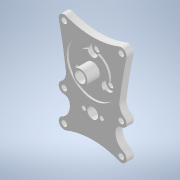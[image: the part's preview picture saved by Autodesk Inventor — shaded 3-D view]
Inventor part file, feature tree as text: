
AUTODESK INVENTOR PART (.ipt)
format: ipt  version: 2022 (Build 260153070, 153G)  size: 269,824 bytes
history: native  units: mm
features: reference x10, extrude x6, other x5, sketch x4
ambient origin geometry x8: Origin, YZ Plane, XZ Plane, XY Plane, X Axis, Y Axis, Z Axis, Center Point
bodies: Solid1 (feature_tree)
feature tree (25):
  extrude  "Extrusion1"  Depth=4.0mm
  sketch  "Sketch2"  dims[d2=4.0mm d3=3.1mm]
  extrude  "Extrusion2"  Depth=4.0mm
  extrude  "Extrusion3"  Depth=1.5mm
  extrude  "Extrusion4"  Depth=1.5mm
  extrude  "Extrusion5"  Depth=4.0mm
  extrude  "Extrusion6"  Depth=4.0mm
  sketch  "Sketch1"  dims[d0=12.3mm d1=4.0mm]
  reference  "Reference1"
  reference  "Reference2"
  reference  "Reference3"
  reference  "Reference5"
  reference  "Reference6"
  reference  "Reference7"
  reference  "Reference8"
  reference  "Reference9"
  reference  "Reference10"
  reference  "Reference11"
  sketch  "Sketch4"  dims[d4=1.5mm d5=3.1mm d6=1.5mm]
  sketch  "Sketch5"  dims[d7=3.1mm d8=1.5mm d9=3.1mm d10=1.5mm d11=32.0mm d12=50.0mm d14=50.0mm d17=4.0mm d18=0.0mm d19=16.0mm d20=37.0mm d21=1.0mm d22=2.0mm d23=0.0mm d24=7.0mm d25=0.0mm d26=1.75mm d27=3.5mm d28=1.0mm d29=0.0mm d30=30.0mm d32=360.0deg d34=2.5mm d35=0.0mm d38=17.25mm d40=1.5mm d42=4.0mm d43=0.0mm d45=25.307274mm]
  other  "<userpath> laptop\Desktop\SumoBot\sumobotLIDAR\sumobotLIDAR.iam"
  other  "sumobotLIDAR.iam"
  other  "SRM-12-06A:1"
  other  "MOTOR:1"
  other  "608ZZ bearing:1"
